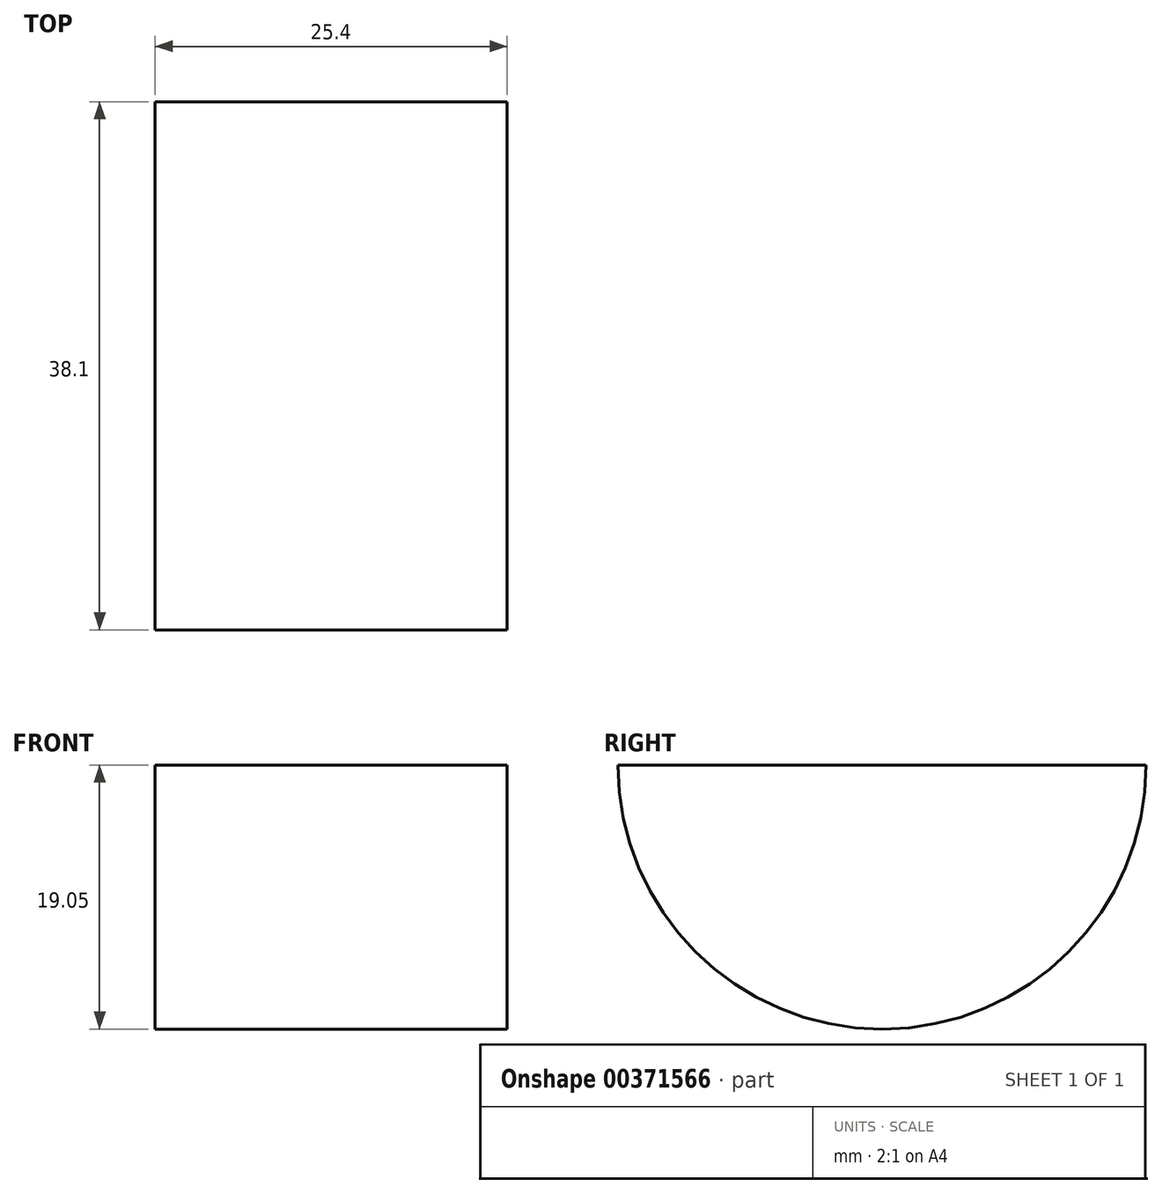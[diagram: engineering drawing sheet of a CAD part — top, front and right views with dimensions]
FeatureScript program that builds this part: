
annotation { "Feature Type Name" : "Feature", "Feature Type Description" : "" }
export const myFeature = defineFeature(function(context is Context, id is Id, definition is map)
    precondition{}
    {
        {
            var Q0;
            Q0=qCreatedBy(makeId("Front.planeOp"),FACE);
            var sketch = newSketch(context, id + "F0", { "sketchPlane" : qUnion([Q0])});
            skLineSegment(sketch, "E0", {"start": v(0, 0) * mm, "end": v(0, 38.1) * mm});
            skLineSegment(sketch, "E1", {"start": v(0, 38.1) * mm, "end": v(25.4, 38.1) * mm});
            skLineSegment(sketch, "E2", {"start": v(25.4, 38.1) * mm, "end": v(25.4, 0) * mm});
            skLineSegment(sketch, "E3", {"start": v(25.4, 0) * mm, "end": v(0, 0) * mm});
            skSolve(sketch);
        }
        {
            var Q0;
            Q0=makeQuery(id+"F0.imprint","IMPRINT",FACE,{"disambiguationData":[TD([[makeQuery(id+"F0.imprint","IMPRINT",EDGE,{"derivedFrom":sQuery(id+"F0.wireOp",EDGE,"E0")}),-1.0]])]});
            extrude(context, id + "F1", {"entities" : qUnion([Q0]), "depth" : 63.5 * mm});
        }
        {
            var Q0;
            Q0=makeQuery(id+"F1.opExtrude","SWEPT_FACE",FACE,{"disambiguationData":[OSD([sQuery(id+"F0.wireOp",EDGE,"E0")])]});
            var sketch = newSketch(context, id + "F2", { "sketchPlane" : qUnion([Q0])});
            skArc(sketch, "E4", {"start": v(50.8, 38.1) * mm, "mid": v(31.75, 19.05) * mm, "end": v(12.7, 38.1) * mm});
            skSolve(sketch);
        }
        {
            var Q0;
            {var subQ0=sQuery(id+"F2.wireOp",EDGE,"E4");Q0=makeQuery(id+"F2.imprint","IMPRINT",FACE,{"disambiguationData":[TD([[makeQuery(id+"F2.imprint","IMPRINT",EDGE,{"derivedFrom":subQ0}),-1.0]])]});}
            extrude(context, id + "F3", {"entities" : qUnion([Q0]), "operationType" : NewBodyOperationType.REMOVE, "oppositeDirection" : true, "depth" : 25.4 * mm});
        }
    });
